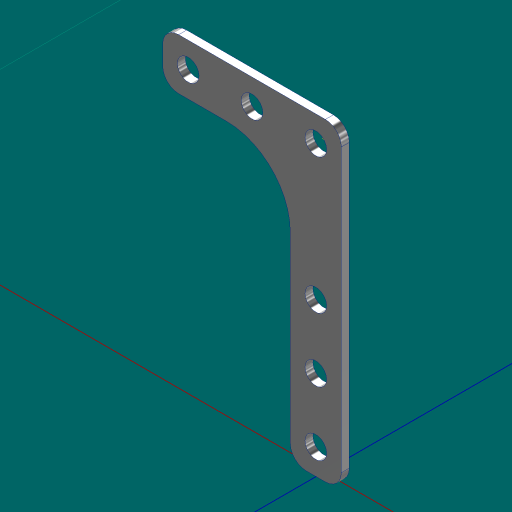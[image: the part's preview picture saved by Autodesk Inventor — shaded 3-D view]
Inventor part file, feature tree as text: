
AUTODESK INVENTOR PART (.ipt)
format: ipt  version: 2023.1 (Build 271208000, 208)  size: 131,584 bytes
history: native  units: in
note: dims shown in document units (in); Inventor stores cm internally (conversion verified against a paired STEP export)
features: fillet x2, extrude x1, sketch x1
ambient origin geometry x8: Origin, YZ Plane, XZ Plane, XY Plane, X Axis, Y Axis, Z Axis, Center Point
bodies: Solid1 (feature_tree)
feature tree (4):
  extrude  "Extrusion1"  Depth=0.0625in TaperAngle=0.0deg
  fillet  "Fillet1"  Radius=1.0607in
  fillet  "Fillet2"  Radius=0.17in
  sketch  "Sketch1"  dims[d3=1.1811in d5=0.5in d6=0.3937in d8=1.0in d19=0.0625in d20=0.0in d21=1.0607in d22=0.17in d23=1.1811in d25=0.5in d26=0.3937in d28=1.0in d30=0.4in d31=0.125in d32=0.5in]
